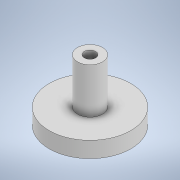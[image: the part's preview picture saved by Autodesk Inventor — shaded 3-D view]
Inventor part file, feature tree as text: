
AUTODESK INVENTOR PART (.ipt)
format: ipt  version: 2022 (Build 260153000, 153)  size: 111,616 bytes
history: native  units: mm
features: extrude x3, sketch x3
ambient origin geometry x8: Origin, YZ Plane, XZ Plane, XY Plane, X Axis, Y Axis, Z Axis, Center Point
bodies: Solid1 (feature_tree)
feature tree (6):
  extrude  "Extrusion1"  Depth=3.5mm TaperAngle=0.0deg
  extrude  "Extrusion2"  Depth=10.0mm TaperAngle=0.0deg
  extrude  "Extrusion3"  Depth=3.5mm TaperAngle=0.0deg
  sketch  "Sketch1"  dims[d0=18.0mm d1=3.5mm d2=0.0mm]
  sketch  "Sketch2"  dims[d3=5.5mm d4=10.0mm d5=0.0mm]
  sketch  "Sketch3"  dims[d6=2.5mm d7=3.5mm d8=0.0mm]
